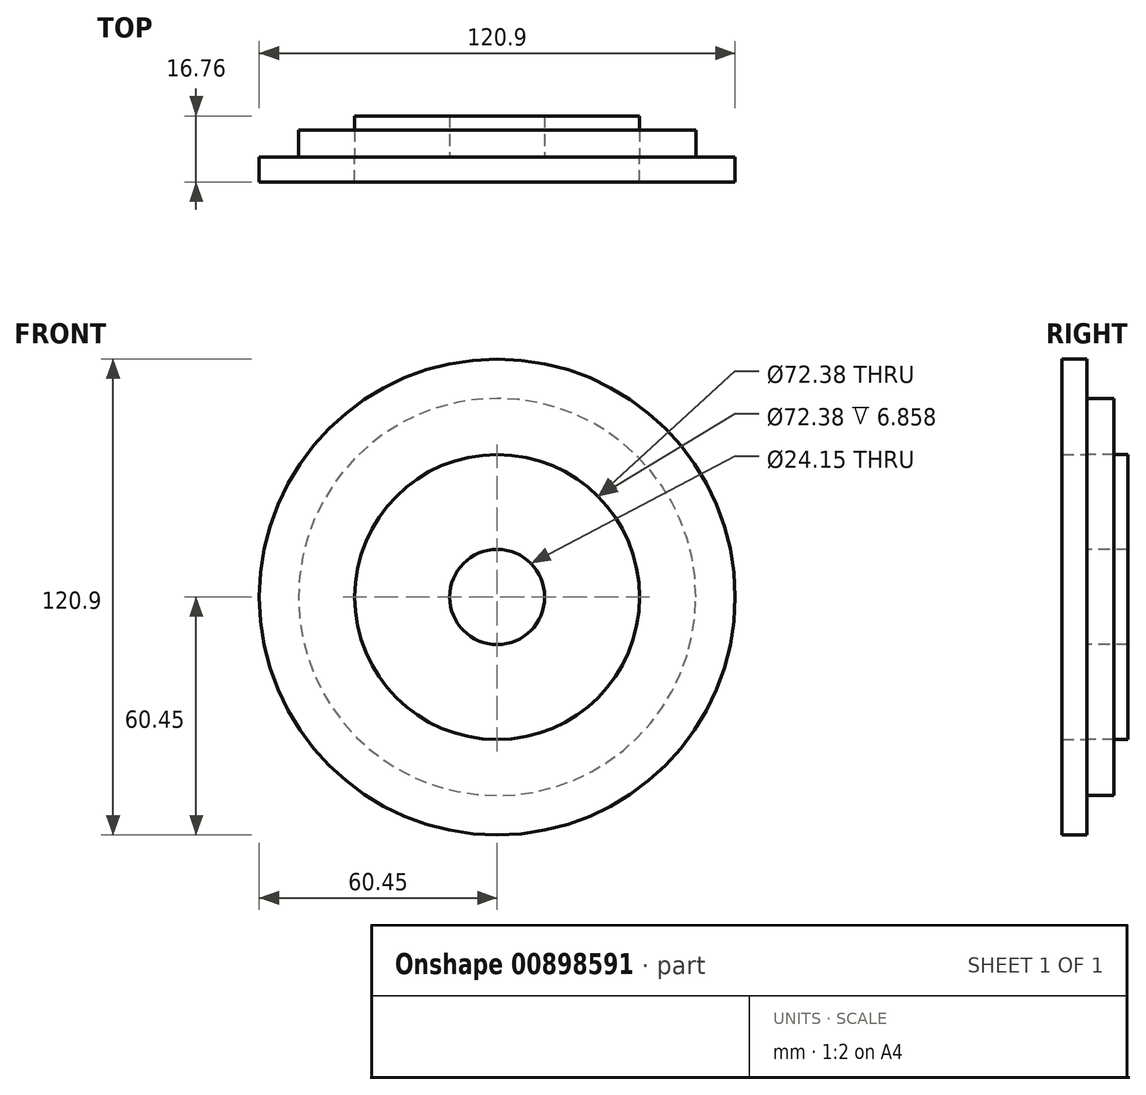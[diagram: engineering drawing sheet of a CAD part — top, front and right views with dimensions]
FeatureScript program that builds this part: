
annotation { "Feature Type Name" : "Feature", "Feature Type Description" : "" }
export const myFeature = defineFeature(function(context is Context, id is Id, definition is map)
    precondition{}
    {
        {
            var Q0;
            Q0=qCreatedBy(makeId("Front.planeOp"),FACE);
            var sketch = newSketch(context, id + "F0", { "sketchPlane" : qUnion([Q0])});
            skCircle(sketch, "E0", {"center": v(0, 0) * mm, "radius": 12.07 * mm});
            skCircle(sketch, "E1", {"center": v(0, 0) * mm, "radius": 36.2 * mm});
            skCircle(sketch, "E2", {"center": v(0, 0) * mm, "radius": 60.45 * mm});
            skSolve(sketch);
        }
        {
            var Q0;
            Q0=makeQuery(id+"F0.imprint","IMPRINT",FACE,{"disambiguationData":[TD([[makeQuery(id+"F0.imprint","IMPRINT",EDGE,{"derivedFrom":sQuery(id+"F0.wireOp",EDGE,"E0")}),-1.0]])]});
            extrude(context, id + "F1", {"entities" : qUnion([Q0]), "oppositeDirection" : true, "depth" : 10.4 * mm, "offsetDistance" : 25.4 * mm});
        }
        {
            var Q0;
            Q0=makeQuery(id+"F0.imprint","IMPRINT",FACE,{"disambiguationData":[TD([[makeQuery(id+"F0.imprint","IMPRINT",EDGE,{"derivedFrom":sQuery(id+"F0.wireOp",EDGE,"E1")}),-1.0]])]});
            extrude(context, id + "F2", {"entities" : qUnion([Q0]), "depth" : 6.35 * mm, "offsetDistance" : 25.4 * mm});
        }
        {
            var Q0;
            Q0=makeQuery(id+"F0.imprint","IMPRINT",FACE,{"disambiguationData":[TD([[makeQuery(id+"F0.imprint","IMPRINT",EDGE,{"derivedFrom":sQuery(id+"F0.wireOp",EDGE,"E1")}),-1.0]])]});
            var sketch = newSketch(context, id + "F3", { "sketchPlane" : qUnion([Q0])});
            skCircle(sketch, "E3", {"center": v(0, 0) * mm, "radius": 50.46 * mm});
            skSolve(sketch);
        }
        {
            var Q0;
            Q0=makeQuery(id+"F3.imprint","IMPRINT",FACE,{"disambiguationData":[TD([[makeQuery(id+"F3.imprint","IMPRINT",EDGE,{"derivedFrom":sQuery(id+"F3.wireOp",EDGE,"E3")}),1.0]])]});
            extrude(context, id + "F4", {"entities" : qUnion([Q0]), "oppositeDirection" : true, "depth" : 6.86 * mm, "offsetDistance" : 25.4 * mm});
        }
    });
